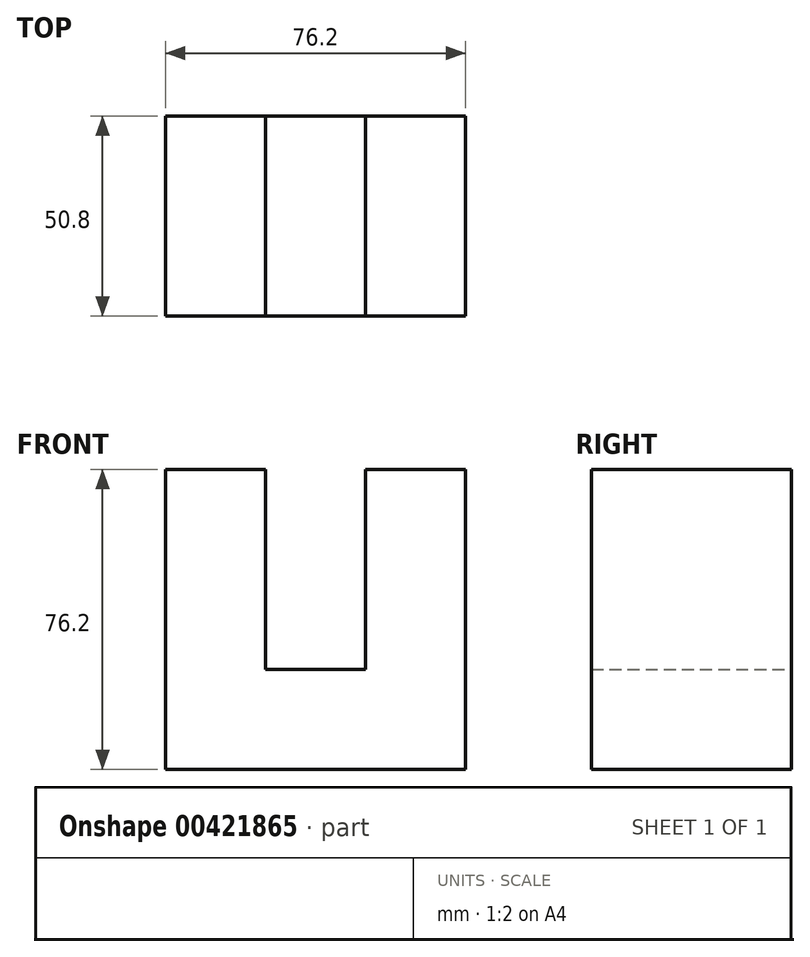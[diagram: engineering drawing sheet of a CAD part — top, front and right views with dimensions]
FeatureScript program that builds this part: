
annotation { "Feature Type Name" : "Feature", "Feature Type Description" : "" }
export const myFeature = defineFeature(function(context is Context, id is Id, definition is map)
    precondition{}
    {
        {
            var Q0;
            Q0=qCreatedBy(makeId("Front.planeOp"),FACE);
            var sketch = newSketch(context, id + "F0", { "sketchPlane" : qUnion([Q0])});
            skLineSegment(sketch, "E0", {"start": v(-37.44, 58) * mm, "end": v(-12.04, 58) * mm});
            skLineSegment(sketch, "E1", {"start": v(-12.04, 58) * mm, "end": v(-12.04, 7.2) * mm});
            skLineSegment(sketch, "E2", {"start": v(-37.44, 58) * mm, "end": v(-37.44, -18.2) * mm});
            skLineSegment(sketch, "E3", {"start": v(-37.44, -18.2) * mm, "end": v(38.76, -18.2) * mm});
            skLineSegment(sketch, "E4", {"start": v(38.76, -18.2) * mm, "end": v(38.76, 58) * mm});
            skLineSegment(sketch, "E5", {"start": v(38.76, 58) * mm, "end": v(13.36, 58) * mm});
            skLineSegment(sketch, "E6", {"start": v(13.36, 58) * mm, "end": v(13.36, 7.2) * mm});
            skLineSegment(sketch, "E7", {"start": v(-12.04, 7.2) * mm, "end": v(13.36, 7.2) * mm});
            skSolve(sketch);
        }
        {
            var Q0;
            Q0=makeQuery(id+"F0.imprint","IMPRINT",FACE,{"disambiguationData":[TD([[makeQuery(id+"F0.imprint","IMPRINT",EDGE,{"derivedFrom":sQuery(id+"F0.wireOp",EDGE,"E0")}),-1.0]])]});
            extrude(context, id + "F1", {"entities" : qUnion([Q0]), "depth" : 50.8 * mm});
        }
    });
